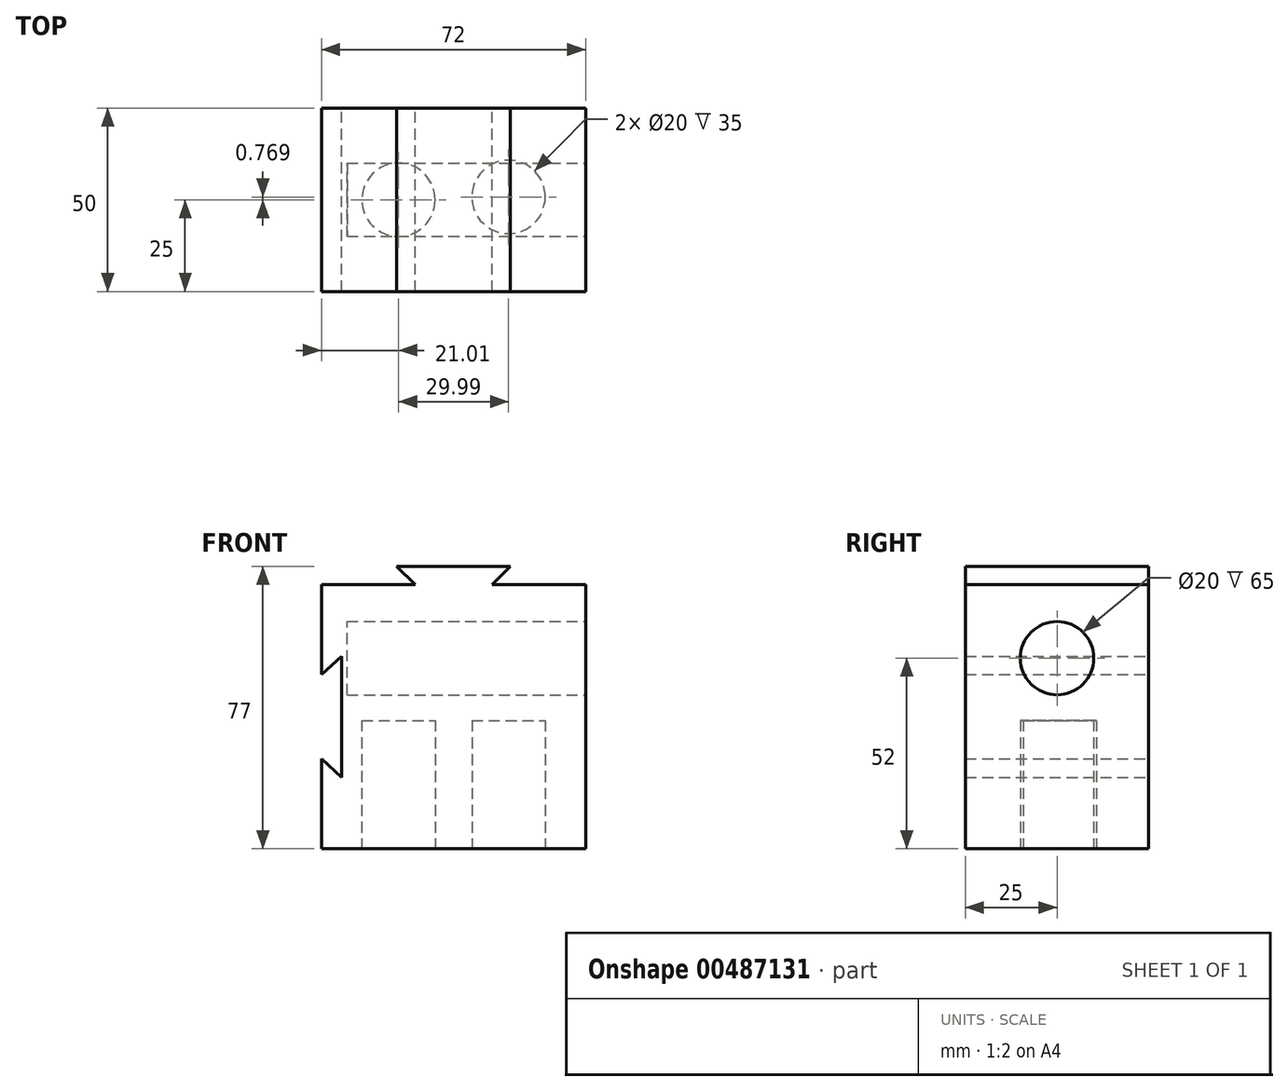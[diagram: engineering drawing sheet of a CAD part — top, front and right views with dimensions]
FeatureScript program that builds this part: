
annotation { "Feature Type Name" : "Feature", "Feature Type Description" : "" }
export const myFeature = defineFeature(function(context is Context, id is Id, definition is map)
    precondition{}
    {
        {
            var Q0;
            Q0=qCreatedBy(makeId("Front.planeOp"),FACE);
            var sketch = newSketch(context, id + "F0", { "sketchPlane" : qUnion([Q0])});
            skLineSegment(sketch, "E0.bottom", {"start": v(0, 0) * mm, "end": v(72, 0) * mm});
            skLineSegment(sketch, "E0.top", {"start": v(0, -72) * mm, "end": v(72, -72) * mm});
            skLineSegment(sketch, "E0.left", {"start": v(0, 0) * mm, "end": v(0, -72) * mm});
            skLineSegment(sketch, "E0.right", {"start": v(72, 0) * mm, "end": v(72, -72) * mm});
            skLineSegment(sketch, "E1", {"start": v(25.5, 0) * mm, "end": v(20.5, 5) * mm});
            skLineSegment(sketch, "E2", {"start": v(20.5, 5) * mm, "end": v(51.5, 5) * mm});
            skLineSegment(sketch, "E3", {"start": v(51.5, 5) * mm, "end": v(46.5, 0) * mm});
            skLineSegment(sketch, "E4", {"start": v(0, -47.5) * mm, "end": v(5.5, -52.5) * mm});
            skLineSegment(sketch, "E5", {"start": v(5.5, -52.5) * mm, "end": v(5.5, -19.5) * mm});
            skLineSegment(sketch, "E6", {"start": v(5.5, -19.5) * mm, "end": v(0, -24.5) * mm});
            skSolve(sketch);
        }
        {
            var Q0;
            {var subQ0=sQuery(id+"F0.wireOp",EDGE,"E1");Q0=makeQuery(id+"F0.imprint","IMPRINT",FACE,{"disambiguationData":[TD([[makeQuery(id+"F0.imprint","IMPRINT",EDGE,{"derivedFrom":subQ0}),-1.0]])]});}
            var Q1;
            {var subQ0=sQuery(id+"F0.wireOp",EDGE,"E0.top");Q1=makeQuery(id+"F0.imprint","IMPRINT",FACE,{"disambiguationData":[TD([[makeQuery(id+"F0.imprint","IMPRINT",EDGE,{"derivedFrom":subQ0}),1.0]])]});}
            extrude(context, id + "F1", {"entities" : qUnion([Q0, Q1]), "depth" : 50 * mm});
        }
        {
            var Q0;
            Q0=makeQuery(id+"F1.opExtrude","SWEPT_FACE",FACE,{"disambiguationData":[OSD([sQuery(id+"F0.wireOp",EDGE,"E0.right")])]});
            var sketch = newSketch(context, id + "F2", { "sketchPlane" : qUnion([Q0])});
            skCircle(sketch, "E7", {"center": v(-25, -20) * mm, "radius": 10 * mm});
            skSolve(sketch);
        }
        {
            var Q0;
            Q0 = qSketchRegion(id + "F2", true);
            extrude(context, id + "F3", {"entities" : qUnion([Q0]), "operationType" : NewBodyOperationType.REMOVE, "oppositeDirection" : true, "depth" : 65 * mm});
        }
        {
            var Q0;
            Q0=makeQuery(id+"F1.opExtrude","SWEPT_FACE",FACE,{"disambiguationData":[OSD([sQuery(id+"F0.wireOp",EDGE,"E0.top")])]});
            var sketch = newSketch(context, id + "F4", { "sketchPlane" : qUnion([Q0])});
            skCircle(sketch, "E8", {"center": v(51, 24.23) * mm, "radius": 10 * mm});
            skCircle(sketch, "E9", {"center": v(21, 25) * mm, "radius": 10 * mm});
            skSolve(sketch);
        }
        {
            var Q0;
            Q0 = qSketchRegion(id + "F4", true);
            extrude(context, id + "F5", {"entities" : qUnion([Q0]), "operationType" : NewBodyOperationType.REMOVE, "oppositeDirection" : true, "depth" : 35 * mm});
        }
    });
